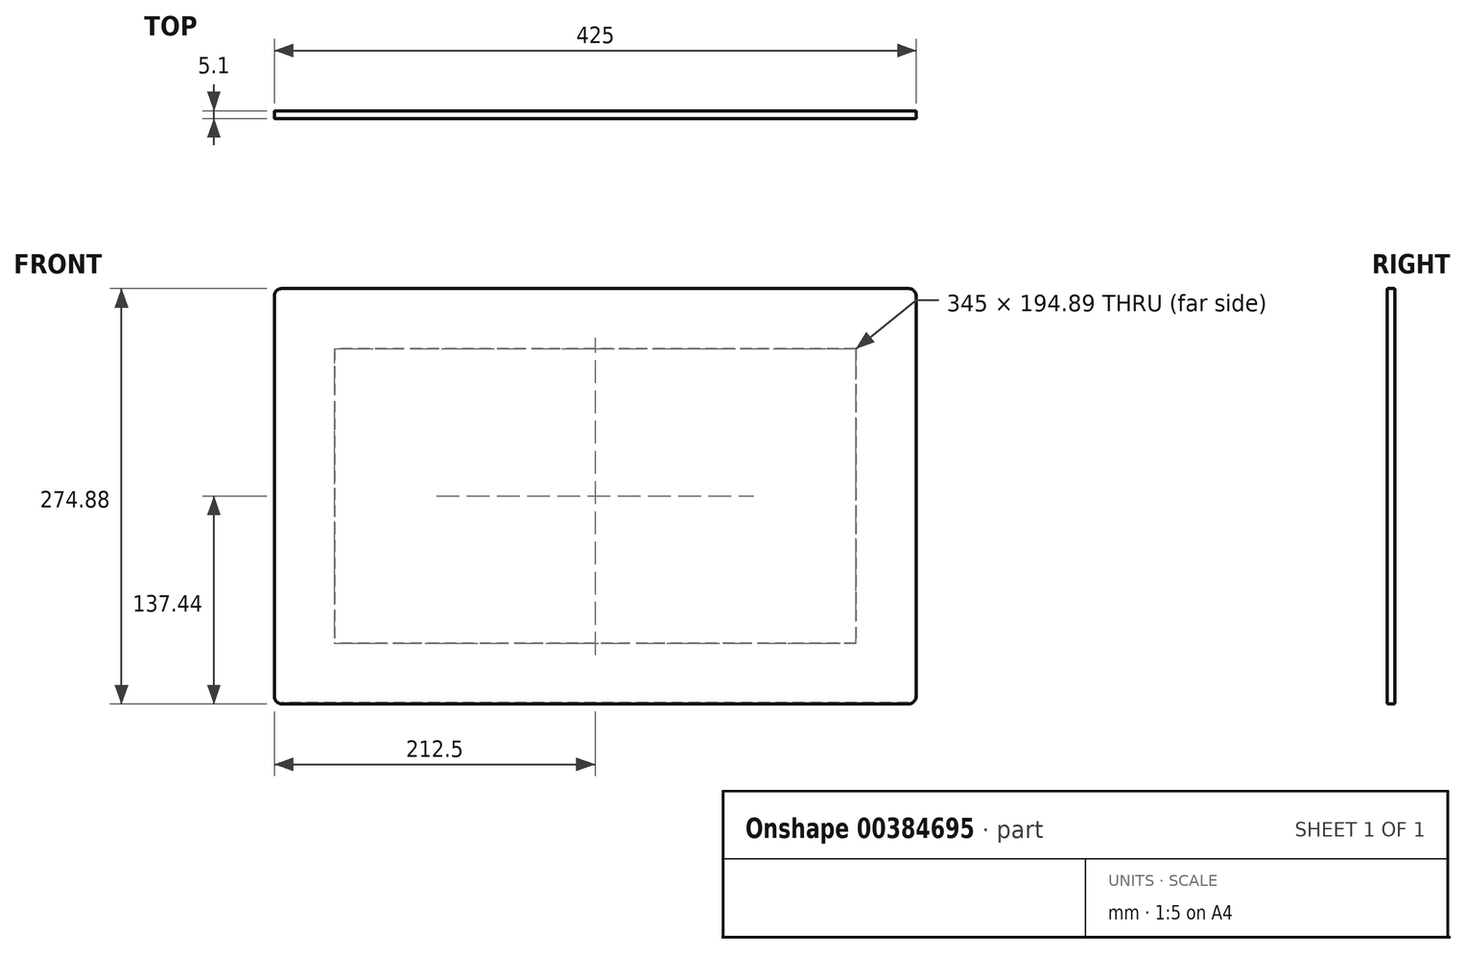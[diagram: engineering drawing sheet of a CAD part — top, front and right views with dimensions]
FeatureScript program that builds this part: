
annotation { "Feature Type Name" : "Feature", "Feature Type Description" : "" }
export const myFeature = defineFeature(function(context is Context, id is Id, definition is map)
    precondition{}
    {
        {
            var Q0;
            Q0=qCreatedBy(makeId("Front.planeOp"),FACE);
            var sketch = newSketch(context, id + "F0", { "sketchPlane" : qUnion([Q0])});
            skLineSegment(sketch, "E0.bottom", {"start": v(172.5, 97.44) * mm, "end": v(-172.5, 97.44) * mm});
            skLineSegment(sketch, "E0.top", {"start": v(172.5, -97.44) * mm, "end": v(-172.5, -97.44) * mm});
            skLineSegment(sketch, "E0.left", {"start": v(172.5, 97.44) * mm, "end": v(172.5, -97.44) * mm});
            skLineSegment(sketch, "E0.right", {"start": v(-172.5, 97.44) * mm, "end": v(-172.5, -97.44) * mm});
            skPoint(sketch, "E0.middle", {"position": v(0, 0) * mm});
            skLineSegment(sketch, "E1.0", {"start": v(212.5, 137.44) * mm, "end": v(-212.5, 137.44) * mm});
            skLineSegment(sketch, "E2.0", {"start": v(212.5, 137.44) * mm, "end": v(212.5, -137.44) * mm});
            skLineSegment(sketch, "E3.0", {"start": v(212.5, -137.44) * mm, "end": v(-212.5, -137.44) * mm});
            skLineSegment(sketch, "E4.0", {"start": v(-212.5, 137.44) * mm, "end": v(-212.5, -137.44) * mm});
            skSolve(sketch);
        }
        {
            var Q0;
            Q0=makeQuery(id+"F0.imprint","IMPRINT",FACE,{"disambiguationData":[TD([[makeQuery(id+"F0.imprint","IMPRINT",EDGE,{"derivedFrom":sQuery(id+"F0.wireOp",EDGE,"E0.bottom")}),1.0]])]});
            var Q1;
            Q1=makeQuery(id+"F0.imprint","IMPRINT",FACE,{"disambiguationData":[TD([[makeQuery(id+"F0.imprint","IMPRINT",EDGE,{"derivedFrom":sQuery(id+"F0.wireOp",EDGE,"E0.bottom")}),-1.0]])]});
            extrude(context, id + "F1", {"entities" : qUnion([Q0, Q1]), "depth" : 5 * mm});
        }
        {
            var Q0;
            Q0=makeQuery(id+"F1.opExtrude","SWEPT_EDGE",EDGE,{"disambiguationData":[OSD([sQuery(id+"F0.wireOp",EDGE,"E1.0"),sQuery(id+"F0.wireOp",EDGE,"E4.0")])]});
            var Q1;
            Q1=makeQuery(id+"F1.opExtrude","SWEPT_EDGE",EDGE,{"disambiguationData":[OSD([sQuery(id+"F0.wireOp",EDGE,"E1.0"),sQuery(id+"F0.wireOp",EDGE,"E2.0")])]});
            var Q2;
            Q2=makeQuery(id+"F1.opExtrude","SWEPT_EDGE",EDGE,{"disambiguationData":[OSD([sQuery(id+"F0.wireOp",EDGE,"E3.0"),sQuery(id+"F0.wireOp",EDGE,"E4.0")])]});
            var Q3;
            Q3=makeQuery(id+"F1.opExtrude","SWEPT_EDGE",EDGE,{"disambiguationData":[OSD([sQuery(id+"F0.wireOp",EDGE,"E2.0"),sQuery(id+"F0.wireOp",EDGE,"E3.0")])]});
            fillet(context, id + "F2", {"entities" : qUnion([Q0, Q1, Q2, Q3]), "radius" : 5 * mm, "tangentPropagation" : true, "allowEdgeOverflow" : false});
        }
        {
            var Q0;
            Q0=makeQuery(id+"F1.opExtrude","CAP_EDGE",EDGE,{"disambiguationData":[OSD([sQuery(id+"F0.wireOp",EDGE,"E4.0")])],"isStart":false});
            var Q1;
            {var subQ0=sQuery(id+"F0.wireOp",EDGE,"E4.0");var subQ1=sQuery(id+"F0.wireOp",EDGE,"E3.0");Q1=makeQuery(id+"F2.opFillet","BLEND_EDGE",EDGE,{"blendedFrom":[makeQuery(id+"F1.opExtrude","SWEPT_EDGE",EDGE,{"disambiguationData":[OSD([subQ1,subQ0])]}),makeQuery(id+"F1.opExtrude","CAP_FACE",FACE,{"disambiguationData":[OSD([sQuery(id+"F0.wireOp",EDGE,"E1.0"),sQuery(id+"F0.wireOp",EDGE,"E2.0"),subQ1,subQ0])],"isStart":true})],"blendedInto":[makeQuery(id+"F1.opExtrude","CAP_FACE",FACE,{"disambiguationData":[OSD([sQuery(id+"F0.wireOp",EDGE,"E1.0"),sQuery(id+"F0.wireOp",EDGE,"E2.0"),subQ1,subQ0])],"isStart":true})]});}
            fillet(context, id + "F3", {"entities" : qUnion([Q0, Q1]), "radius" : 0.5 * mm, "tangentPropagation" : true, "allowEdgeOverflow" : false});
        }
        {
            var Q0;
            Q0=makeQuery(id+"F0.imprint","IMPRINT",FACE,{"disambiguationData":[TD([[makeQuery(id+"F0.imprint","IMPRINT",EDGE,{"derivedFrom":sQuery(id+"F0.wireOp",EDGE,"E0.bottom")}),-1.0]])]});
            var sketch = newSketch(context, id + "F4", { "sketchPlane" : qUnion([Q0])});
            skLineSegment(sketch, "E5.bottom", {"start": v(172.5, -97.44) * mm, "end": v(-172.5, -97.44) * mm});
            skLineSegment(sketch, "E5.top", {"start": v(172.5, 97.44) * mm, "end": v(-172.5, 97.44) * mm});
            skLineSegment(sketch, "E5.left", {"start": v(172.5, -97.44) * mm, "end": v(172.5, 97.44) * mm});
            skLineSegment(sketch, "E5.right", {"start": v(-172.5, -97.44) * mm, "end": v(-172.5, 97.44) * mm});
            skLineSegment(sketch, "E6.bottom", {"start": v(212, 136.94) * mm, "end": v(-212, 136.94) * mm});
            skLineSegment(sketch, "E6.top", {"start": v(212, -136.94) * mm, "end": v(-212, -136.94) * mm});
            skLineSegment(sketch, "E6.left", {"start": v(212, 136.94) * mm, "end": v(212, -136.94) * mm});
            skLineSegment(sketch, "E6.right", {"start": v(-212, 136.94) * mm, "end": v(-212, -136.94) * mm});
            skSolve(sketch);
        }
        {
            var Q0;
            Q0 = qSketchRegion(id + "F4", true);
            extrude(context, id + "F5", {"entities" : qUnion([Q0]), "oppositeDirection" : true, "depth" : 0.1 * mm});
        }
        {
            var Q0;
            Q0=makeQuery(id+"F5.opExtrude","SWEPT_EDGE",EDGE,{"disambiguationData":[OSD([sQuery(id+"F4.wireOp",EDGE,"E6.top"),sQuery(id+"F4.wireOp",EDGE,"E6.right")])]});
            var Q1;
            Q1=makeQuery(id+"F5.opExtrude","SWEPT_EDGE",EDGE,{"disambiguationData":[OSD([sQuery(id+"F4.wireOp",EDGE,"E6.top"),sQuery(id+"F4.wireOp",EDGE,"E6.left")])]});
            var Q2;
            Q2=makeQuery(id+"F5.opExtrude","SWEPT_EDGE",EDGE,{"disambiguationData":[OSD([sQuery(id+"F4.wireOp",EDGE,"E6.bottom"),sQuery(id+"F4.wireOp",EDGE,"E6.left")])]});
            var Q3;
            Q3=makeQuery(id+"F5.opExtrude","SWEPT_EDGE",EDGE,{"disambiguationData":[OSD([sQuery(id+"F4.wireOp",EDGE,"E6.bottom"),sQuery(id+"F4.wireOp",EDGE,"E6.right")])]});
            fillet(context, id + "F6", {"entities" : qUnion([Q0, Q1, Q2, Q3]), "radius" : 4.5 * mm, "tangentPropagation" : true, "allowEdgeOverflow" : false});
        }
    });
